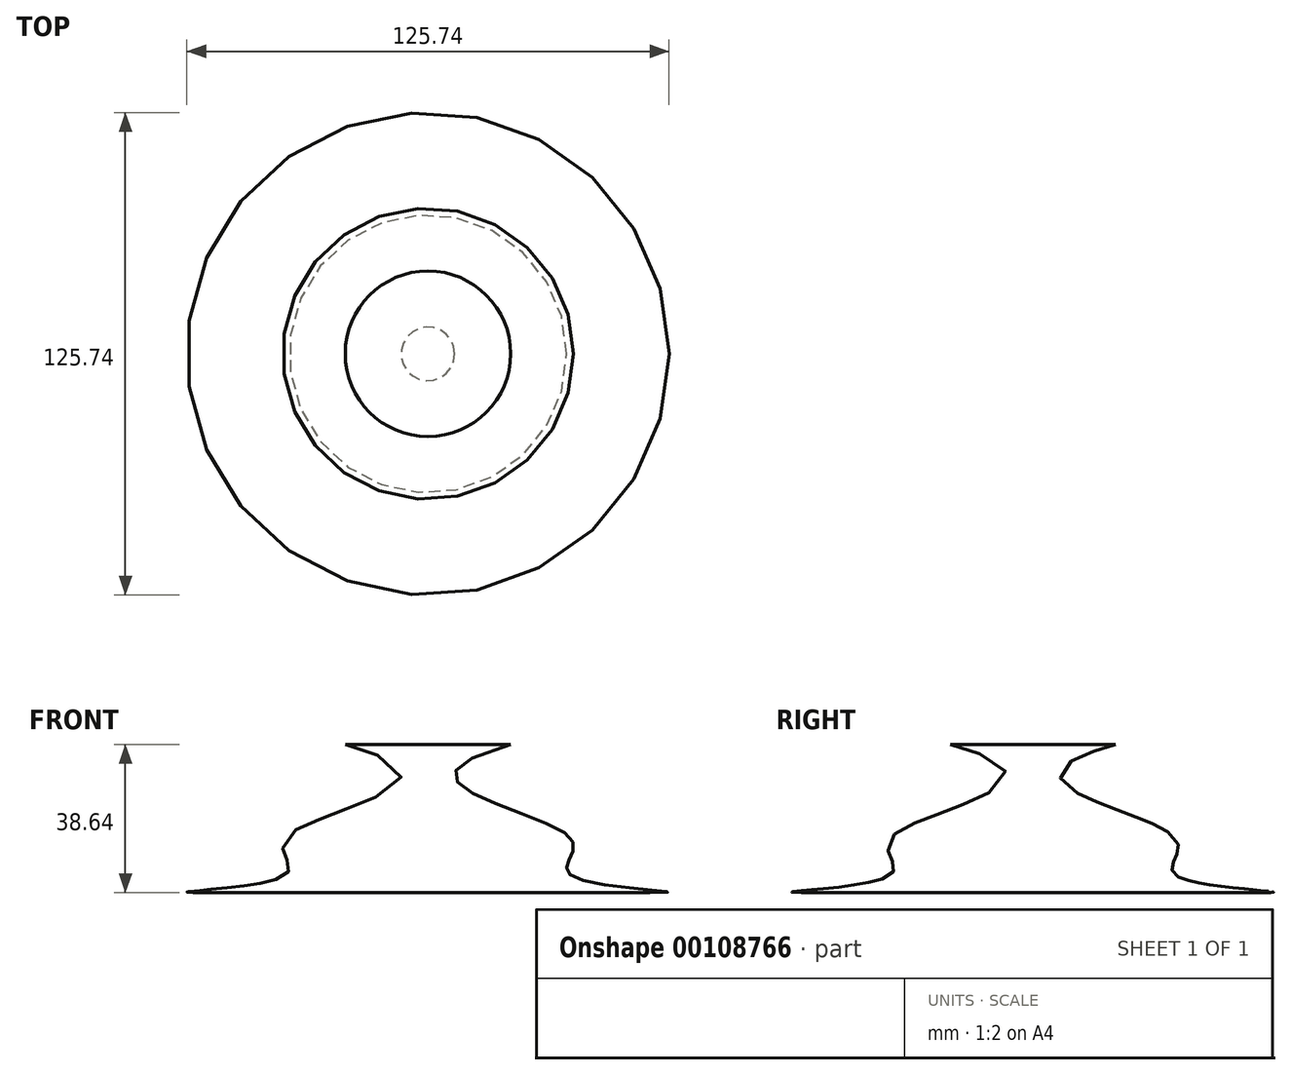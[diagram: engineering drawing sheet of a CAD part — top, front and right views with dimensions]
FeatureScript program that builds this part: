
annotation { "Feature Type Name" : "Feature", "Feature Type Description" : "" }
export const myFeature = defineFeature(function(context is Context, id is Id, definition is map)
    precondition{}
    {
        {
            var Q0;
            Q0=qCreatedBy(makeId("Front.planeOp"),FACE);
            var sketch = newSketch(context, id + "F0", { "sketchPlane" : qUnion([Q0])});
            skLineSegment(sketch, "E0", {"start": v(0, 0) * mm, "end": v(0, 38.59) * mm});
            skLineSegment(sketch, "E1", {"start": v(0, 38.59) * mm, "end": v(21.57, 38.59) * mm});
            skFitSpline(sketch, "E2", {"points": [v(0, 0) * mm, v(38, 4.03) * mm, v(36.15, 15.22) * mm, v(21.57, 38.59) * mm], "startDerivative": vector(762.56, 0) * mm, "endDerivative": vector(309.74, 84.29) * mm});
            skSolve(sketch);
        }
        {
            var Q0;
            Q0=qCreatedBy(makeId("Front.planeOp"),FACE);
            var sketch = newSketch(context, id + "F1", { "sketchPlane" : qUnion([Q0])});
            skLineSegment(sketch, "E3", {"start": v(0, 0) * mm, "end": v(0, 74.93) * mm, "construction": true});
            skSolve(sketch);
        }
        {
            var Q0;
            Q0=makeQuery(id+"F0.imprint","IMPRINT",FACE,{"disambiguationData":[TD([[makeQuery(id+"F0.imprint","IMPRINT",EDGE,{"derivedFrom":sQuery(id+"F0.wireOp",EDGE,"E0")}),-1.0]])]});
            var Q1;
            Q1=sQuery(id+"F1.wireOp",EDGE,"E3");
            revolve(context, id + "F2", {"entities" : qUnion([Q0]), "axis" : qUnion([Q1]), "revolveType" : RevolveType.FULL});
        }
    });
